# Revit family: FU_Chair_Sandler_Woodlook 1-8
name_source: partatom
category: Furniture
units: mm (PartAtom-declared; Revit-internal decimal feet)

## family parameters
Always vertical = Yes
Cut with Voids When Loaded = No
OmniClass Number = 23.40.20.00
OmniClass Title = General Furniture and Specialties
Room Calculation Point = No
Shared = No
Work Plane-Based = No

## types (1)
- FU_Chair_Sandler_Woodlook 1-8
    D = 590 mm  [stored 1.9357 ft]
    Default Elevation = 0 mm  [stored 0 ft]
    Description = Woodlook side chair with frame manufactured entirely from aluminum but with realistic appearance of wood. Highly durable and scratch resistant. Stacks 5.
    H = 955 mm  [stored 3.1332 ft]
    Manufacturer = Sandler
    Model = Woddlokk 1.8
    URL = https://www.sandlerseating.com
    Upholstery = Fabric - Gravity - Frost CPC32
    W = 530 mm  [stored 1.73885 ft]
    Woodlook = Woodlook - 21A Teak

note: [stored X ft] marks values corroborated as IEEE doubles in the binary element streams (Revit-internal decimal feet)

## geometry (parser evidence)
native form markers: Sweep x5
no freeform markers — native parametric forms only
